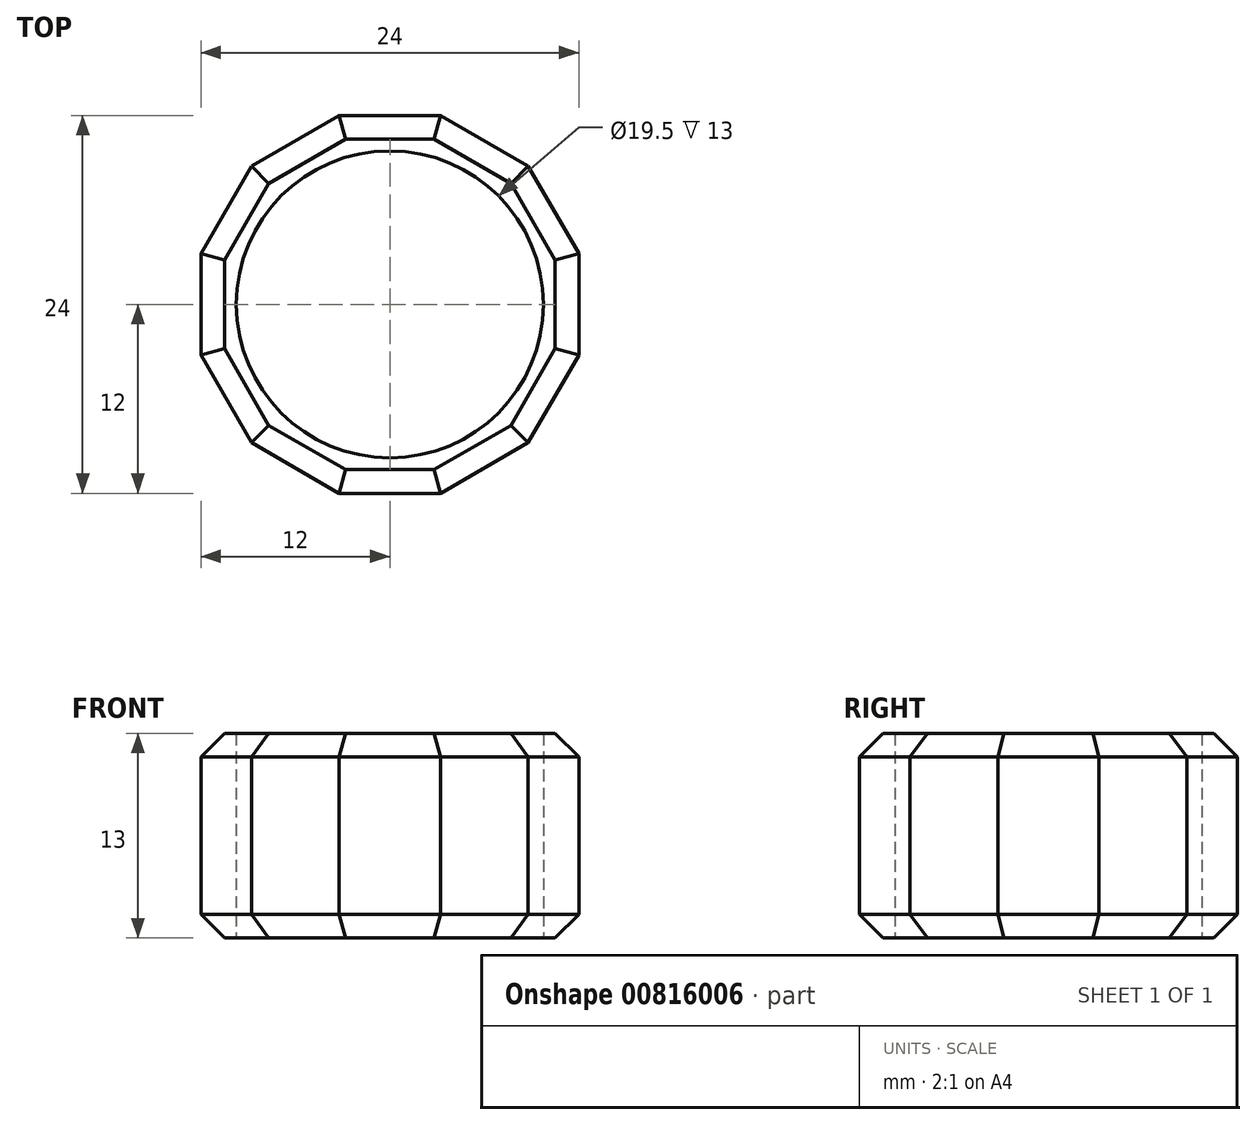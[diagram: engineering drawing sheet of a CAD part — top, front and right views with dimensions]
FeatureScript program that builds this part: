
annotation { "Feature Type Name" : "Feature", "Feature Type Description" : "" }
export const myFeature = defineFeature(function(context is Context, id is Id, definition is map)
    precondition{}
    {
        {
            var Q0;
            Q0=qCreatedBy(makeId("Top.planeOp"),FACE);
            var sketch = newSketch(context, id + "F0", { "sketchPlane" : qUnion([Q0])});
            skCircle(sketch, "E0", {"center": v(0, 0) * mm, "radius": 9.75 * mm});
            skCircle(sketch, "E1.cCircle", {"center": v(0, 0) * mm, "radius": 12 * mm, "construction": true});
            skLineSegment(sketch, "E1.0", {"start": v(12, 3.22) * mm, "end": v(12, -3.22) * mm});
            skLineSegment(sketch, "E1.1", {"start": v(12, -3.22) * mm, "end": v(8.78, -8.78) * mm});
            skLineSegment(sketch, "E1.2", {"start": v(8.78, -8.78) * mm, "end": v(3.22, -12) * mm});
            skLineSegment(sketch, "E1.3", {"start": v(3.22, -12) * mm, "end": v(-3.22, -12) * mm});
            skLineSegment(sketch, "E1.4", {"start": v(-3.22, -12) * mm, "end": v(-8.78, -8.78) * mm});
            skLineSegment(sketch, "E1.5", {"start": v(-8.78, -8.78) * mm, "end": v(-12, -3.22) * mm});
            skLineSegment(sketch, "E1.6", {"start": v(-12, -3.22) * mm, "end": v(-12, 3.22) * mm});
            skLineSegment(sketch, "E1.7", {"start": v(-12, 3.22) * mm, "end": v(-8.78, 8.78) * mm});
            skLineSegment(sketch, "E1.8", {"start": v(-8.78, 8.78) * mm, "end": v(-3.22, 12) * mm});
            skLineSegment(sketch, "E1.9", {"start": v(-3.22, 12) * mm, "end": v(3.22, 12) * mm});
            skLineSegment(sketch, "E1.10", {"start": v(3.22, 12) * mm, "end": v(8.78, 8.78) * mm});
            skLineSegment(sketch, "E1.11", {"start": v(8.78, 8.78) * mm, "end": v(12, 3.22) * mm});
            skPoint(sketch, "E1.0.midPoint", {"position": v(12, 0) * mm});
            skSolve(sketch);
        }
        {
            var Q0;
            Q0=makeQuery(id+"F0.imprint","IMPRINT",FACE,{"disambiguationData":[TD([[makeQuery(id+"F0.imprint","IMPRINT",EDGE,{"derivedFrom":sQuery(id+"F0.wireOp",EDGE,"E0")}),-1.0]])]});
            extrude(context, id + "F1", {"entities" : qUnion([Q0]), "depth" : 13 * mm, "offsetDistance" : 25 * mm});
        }
        {
            var Q0;
            Q0=makeQuery(id+"F1.opExtrude","CAP_EDGE",EDGE,{"disambiguationData":[OSD([sQuery(id+"F0.wireOp",EDGE,"E1.2")])],"isStart":false});
            var Q1;
            Q1=makeQuery(id+"F1.opExtrude","CAP_EDGE",EDGE,{"disambiguationData":[OSD([sQuery(id+"F0.wireOp",EDGE,"E1.1")])],"isStart":false});
            var Q2;
            Q2=makeQuery(id+"F1.opExtrude","CAP_EDGE",EDGE,{"disambiguationData":[OSD([sQuery(id+"F0.wireOp",EDGE,"E1.0")])],"isStart":false});
            var Q3;
            Q3=makeQuery(id+"F1.opExtrude","CAP_EDGE",EDGE,{"disambiguationData":[OSD([sQuery(id+"F0.wireOp",EDGE,"E1.11")])],"isStart":false});
            var Q4;
            Q4=makeQuery(id+"F1.opExtrude","CAP_EDGE",EDGE,{"disambiguationData":[OSD([sQuery(id+"F0.wireOp",EDGE,"E1.10")])],"isStart":false});
            var Q5;
            Q5=makeQuery(id+"F1.opExtrude","CAP_EDGE",EDGE,{"disambiguationData":[OSD([sQuery(id+"F0.wireOp",EDGE,"E1.9")])],"isStart":false});
            var Q6;
            Q6=makeQuery(id+"F1.opExtrude","CAP_EDGE",EDGE,{"disambiguationData":[OSD([sQuery(id+"F0.wireOp",EDGE,"E1.8")])],"isStart":false});
            var Q7;
            Q7=makeQuery(id+"F1.opExtrude","CAP_EDGE",EDGE,{"disambiguationData":[OSD([sQuery(id+"F0.wireOp",EDGE,"E1.7")])],"isStart":false});
            var Q8;
            Q8=makeQuery(id+"F1.opExtrude","CAP_EDGE",EDGE,{"disambiguationData":[OSD([sQuery(id+"F0.wireOp",EDGE,"E1.6")])],"isStart":false});
            var Q9;
            Q9=makeQuery(id+"F1.opExtrude","CAP_EDGE",EDGE,{"disambiguationData":[OSD([sQuery(id+"F0.wireOp",EDGE,"E1.5")])],"isStart":false});
            var Q10;
            Q10=makeQuery(id+"F1.opExtrude","CAP_EDGE",EDGE,{"disambiguationData":[OSD([sQuery(id+"F0.wireOp",EDGE,"E1.4")])],"isStart":false});
            var Q11;
            Q11=makeQuery(id+"F1.opExtrude","CAP_EDGE",EDGE,{"disambiguationData":[OSD([sQuery(id+"F0.wireOp",EDGE,"E1.3")])],"isStart":false});
            var Q12;
            Q12=makeQuery(id+"F1.opExtrude","CAP_EDGE",EDGE,{"disambiguationData":[OSD([sQuery(id+"F0.wireOp",EDGE,"E1.0")])],"isStart":true});
            var Q13;
            Q13=makeQuery(id+"F1.opExtrude","CAP_EDGE",EDGE,{"disambiguationData":[OSD([sQuery(id+"F0.wireOp",EDGE,"E1.11")])],"isStart":true});
            var Q14;
            Q14=makeQuery(id+"F1.opExtrude","CAP_EDGE",EDGE,{"disambiguationData":[OSD([sQuery(id+"F0.wireOp",EDGE,"E1.10")])],"isStart":true});
            var Q15;
            Q15=makeQuery(id+"F1.opExtrude","CAP_EDGE",EDGE,{"disambiguationData":[OSD([sQuery(id+"F0.wireOp",EDGE,"E1.9")])],"isStart":true});
            var Q16;
            Q16=makeQuery(id+"F1.opExtrude","CAP_EDGE",EDGE,{"disambiguationData":[OSD([sQuery(id+"F0.wireOp",EDGE,"E1.8")])],"isStart":true});
            var Q17;
            Q17=makeQuery(id+"F1.opExtrude","CAP_EDGE",EDGE,{"disambiguationData":[OSD([sQuery(id+"F0.wireOp",EDGE,"E1.7")])],"isStart":true});
            var Q18;
            Q18=makeQuery(id+"F1.opExtrude","CAP_EDGE",EDGE,{"disambiguationData":[OSD([sQuery(id+"F0.wireOp",EDGE,"E1.6")])],"isStart":true});
            var Q19;
            Q19=makeQuery(id+"F1.opExtrude","CAP_EDGE",EDGE,{"disambiguationData":[OSD([sQuery(id+"F0.wireOp",EDGE,"E1.5")])],"isStart":true});
            var Q20;
            Q20=makeQuery(id+"F1.opExtrude","CAP_EDGE",EDGE,{"disambiguationData":[OSD([sQuery(id+"F0.wireOp",EDGE,"E1.4")])],"isStart":true});
            var Q21;
            Q21=makeQuery(id+"F1.opExtrude","CAP_EDGE",EDGE,{"disambiguationData":[OSD([sQuery(id+"F0.wireOp",EDGE,"E1.3")])],"isStart":true});
            var Q22;
            Q22=makeQuery(id+"F1.opExtrude","CAP_EDGE",EDGE,{"disambiguationData":[OSD([sQuery(id+"F0.wireOp",EDGE,"E1.2")])],"isStart":true});
            var Q23;
            Q23=makeQuery(id+"F1.opExtrude","CAP_EDGE",EDGE,{"disambiguationData":[OSD([sQuery(id+"F0.wireOp",EDGE,"E1.1")])],"isStart":true});
            chamfer(context, id + "F2", {"entities" : qUnion([Q0, Q1, Q2, Q3, Q4, Q5, Q6, Q7, Q8, Q9, Q10, Q11, Q12, Q13, Q14, Q15, Q16, Q17, Q18, Q19, Q20, Q21, Q22, Q23]), "width" : 1.5 * mm, "tangentPropagation" : true});
        }
    });
